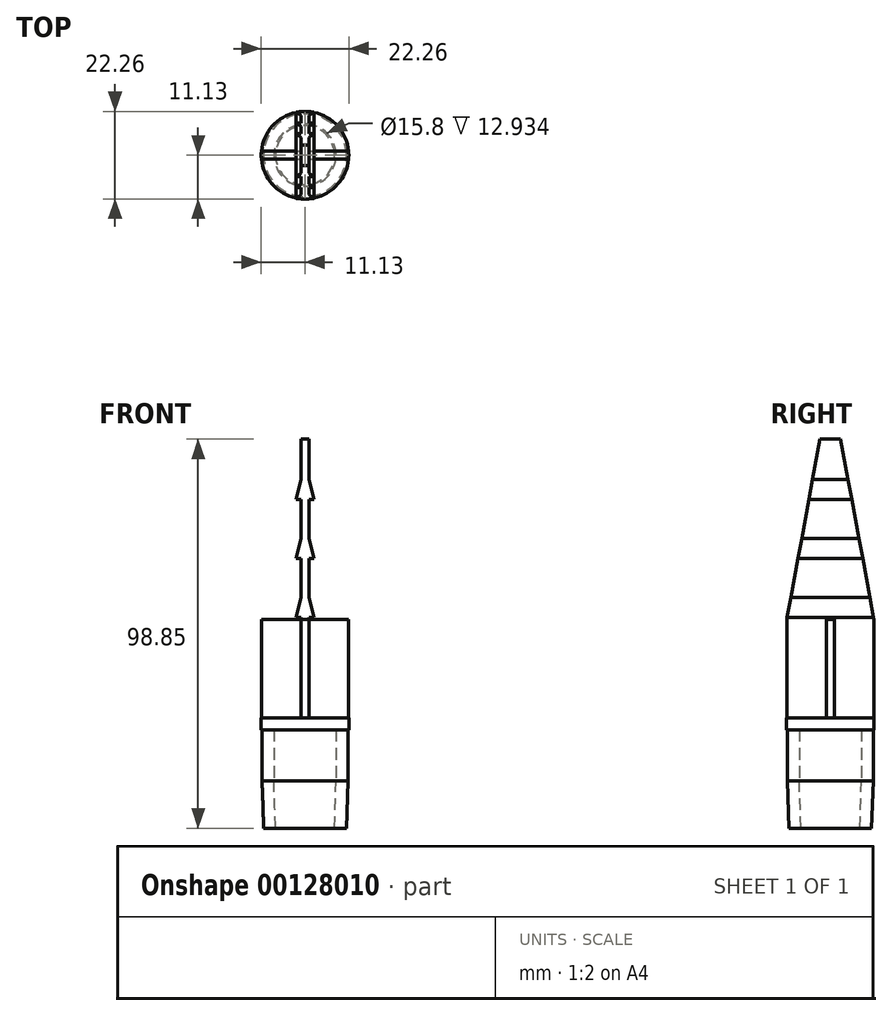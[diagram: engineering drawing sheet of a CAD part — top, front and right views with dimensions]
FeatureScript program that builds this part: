
annotation { "Feature Type Name" : "Feature", "Feature Type Description" : "" }
export const myFeature = defineFeature(function(context is Context, id is Id, definition is map)
    precondition{}
    {
        {
            var Q0;
            Q0=qCreatedBy(makeId("Top.planeOp"),FACE);
            var sketch = newSketch(context, id + "F0", { "sketchPlane" : qUnion([Q0])});
            skCircle(sketch, "E0", {"center": v(0, 0) * mm, "radius": 11.12 * mm});
            skSolve(sketch);
        }
        {
            var Q0;
            Q0=makeQuery(id+"F0.imprint","IMPRINT",FACE,{"disambiguationData":[TD([[makeQuery(id+"F0.imprint","IMPRINT",EDGE,{"derivedFrom":sQuery(id+"F0.wireOp",EDGE,"E0")}),1.0]])]});
            extrude(context, id + "F1", {"entities" : qUnion([Q0]), "depth" : 3 * mm});
        }
        {
            var Q0;
            Q0=makeQuery(id+"F1.opExtrude","CAP_FACE",FACE,{"disambiguationData":[OSD([sQuery(id+"F0.wireOp",EDGE,"E0")])],"isStart":false});
            var sketch = newSketch(context, id + "F2", { "sketchPlane" : qUnion([Q0])});
            skLineSegment(sketch, "E1.bottom", {"start": v(-11.08, 1) * mm, "end": v(-1, 1) * mm});
            skLineSegment(sketch, "E1.top", {"start": v(-11.08, -1) * mm, "end": v(-1, -1) * mm});
            skLineSegment(sketch, "E1.left", {"start": v(-11.08, 1) * mm, "end": v(-11.08, -1) * mm});
            skLineSegment(sketch, "E1.right", {"start": v(11.08, 1) * mm, "end": v(11.08, -1) * mm});
            skPoint(sketch, "E1.middle", {"position": v(0, 0) * mm});
            skLineSegment(sketch, "E2.bottom", {"start": v(-1, 11.08) * mm, "end": v(1, 11.08) * mm});
            skLineSegment(sketch, "E2.top", {"start": v(-1, -11.08) * mm, "end": v(1, -11.08) * mm});
            skLineSegment(sketch, "E2.left", {"start": v(-1, 11.08) * mm, "end": v(-1, 1) * mm});
            skLineSegment(sketch, "E2.right", {"start": v(1, 11.08) * mm, "end": v(1, 1) * mm});
            skLineSegment(sketch, "E3.trimOffspring", {"start": v(-1, -1) * mm, "end": v(-1, -11.08) * mm});
            skLineSegment(sketch, "E4.trimOffspring", {"start": v(1, -1) * mm, "end": v(11.08, -1) * mm});
            skLineSegment(sketch, "E5.trimOffspring", {"start": v(1, -1) * mm, "end": v(1, -11.08) * mm});
            skLineSegment(sketch, "E6.trimOffspring", {"start": v(1, 1) * mm, "end": v(11.08, 1) * mm});
            skSolve(sketch);
        }
        {
            var Q0;
            Q0=makeQuery(id+"F2.imprint","IMPRINT",FACE,{"disambiguationData":[TD([[makeQuery(id+"F2.imprint","IMPRINT",EDGE,{"derivedFrom":sQuery(id+"F2.wireOp",EDGE,"E1.bottom")}),-1.0]])]});
            extrude(context, id + "F3", {"entities" : qUnion([Q0]), "operationType" : NewBodyOperationType.ADD, "depth" : 25 * mm});
        }
        {
            var Q0;
            Q0=makeQuery(id+"F3.opExtrude","SWEPT_FACE",FACE,{"disambiguationData":[OSD([sQuery(id+"F2.wireOp",EDGE,"E5.trimOffspring")])]});
            var sketch = newSketch(context, id + "F4", { "sketchPlane" : qUnion([Q0])});
            skLineSegment(sketch, "E7", {"start": v(-11.08, 28) * mm, "end": v(-2.61, 73.85) * mm});
            skLineSegment(sketch, "E8", {"start": v(2.61, 73.85) * mm, "end": v(11.08, 28) * mm});
            skLineSegment(sketch, "E9", {"start": v(11.08, 28) * mm, "end": v(-11.08, 28) * mm});
            skLineSegment(sketch, "E10", {"start": v(-2.61, 73.85) * mm, "end": v(2.61, 73.85) * mm});
            skPoint(sketch, "E11.orphan", {"position": v(0, 88) * mm});
            skSolve(sketch);
        }
        {
            var Q0;
            {var subQ0=sQuery(id+"F4.wireOp",EDGE,"E7");Q0=makeQuery(id+"F4.imprint","IMPRINT",FACE,{"disambiguationData":[TD([[makeQuery(id+"F4.imprint","IMPRINT",EDGE,{"derivedFrom":subQ0}),-1.0]])]});}
            extrude(context, id + "F5", {"entities" : qUnion([Q0]), "operationType" : NewBodyOperationType.ADD, "oppositeDirection" : true, "depth" : 2 * mm});
        }
        {
            var Q0;
            Q0=qCreatedBy(makeId("Right.planeOp"),FACE);
            var sketch = newSketch(context, id + "F6", { "sketchPlane" : qUnion([Q0])});
            skLineSegment(sketch, "E12", {"start": v(0, 0) * mm, "end": v(0, 19.03) * mm, "construction": true});
            skSolve(sketch);
        }
        {
            var Q0;
            Q0=qCreatedBy(makeId("Front.planeOp"),FACE);
            var sketch = newSketch(context, id + "F7", { "sketchPlane" : qUnion([Q0])});
            skLineSegment(sketch, "E13", {"start": v(0, 37.5) * mm, "end": v(-2.3, 28.53) * mm});
            skLineSegment(sketch, "E14", {"start": v(-2.3, 28.53) * mm, "end": v(2.3, 28.53) * mm});
            skLineSegment(sketch, "E15", {"start": v(2.3, 28.53) * mm, "end": v(0, 37.5) * mm});
            skLineSegment(sketch, "E16.0.1.0", {"start": v(0, 52.5) * mm, "end": v(-2.3, 43.53) * mm});
            skLineSegment(sketch, "E16.0.1.1", {"start": v(2.3, 43.53) * mm, "end": v(0, 52.5) * mm});
            skLineSegment(sketch, "E16.0.1.2", {"start": v(-2.3, 43.53) * mm, "end": v(2.3, 43.53) * mm});
            skLineSegment(sketch, "E16.0.2.0", {"start": v(0, 67.5) * mm, "end": v(-2.3, 58.53) * mm});
            skLineSegment(sketch, "E16.0.2.1", {"start": v(2.3, 58.53) * mm, "end": v(0, 67.5) * mm});
            skLineSegment(sketch, "E16.0.2.2", {"start": v(-2.3, 58.53) * mm, "end": v(2.3, 58.53) * mm});
            skLineSegment(sketch, "E16.direction1", {"start": v(-2.3, 28.53) * mm, "end": v(-27.3, 28.53) * mm, "construction": true});
            skLineSegment(sketch, "E16.direction2", {"start": v(-2.3, 28.53) * mm, "end": v(-2.3, 43.53) * mm, "construction": true});
            skSolve(sketch);
        }
        {
            var Q0;
            Q0 = qSketchRegion(id + "F7", true);
            var Q1;
            Q1=makeQuery(id+"F5.opExtrude","SWEPT_FACE",FACE,{"disambiguationData":[OSD([sQuery(id+"F4.wireOp",EDGE,"E7")])]});
            var Q2;
            Q2=makeQuery(id+"F5.opExtrude","SWEPT_FACE",FACE,{"disambiguationData":[OSD([sQuery(id+"F4.wireOp",EDGE,"E8")])]});
            extrude(context, id + "F8", {"entities" : qUnion([Q0]), "operationType" : NewBodyOperationType.ADD, "endBound" : BoundingType.UP_TO_SURFACE, "endBoundEntityFace" : qUnion([Q1]), "depth" : 25 * mm, "hasSecondDirection" : true, "secondDirectionBound" : SecondDirectionBoundingType.UP_TO_SURFACE, "secondDirectionOppositeDirection" : true, "secondDirectionBoundEntityFace" : qUnion([Q2]), "secondDirectionDepth" : 25 * mm});
        }
        {
            var Q0;
            Q0=qCreatedBy(makeId("Front.planeOp"),FACE);
            var sketch = newSketch(context, id + "F9", { "sketchPlane" : qUnion([Q0])});
            skLineSegment(sketch, "E17", {"start": v(10.9, 0) * mm, "end": v(10.9, -12.93) * mm});
            skLineSegment(sketch, "E18", {"start": v(10.9, -12.93) * mm, "end": v(10.5, -25) * mm});
            skLineSegment(sketch, "E19", {"start": v(10.5, -25) * mm, "end": v(7.5, -25) * mm});
            skLineSegment(sketch, "E20", {"start": v(7.5, -25) * mm, "end": v(7.9, -12.93) * mm});
            skLineSegment(sketch, "E21", {"start": v(7.9, -12.93) * mm, "end": v(7.9, 0) * mm});
            skLineSegment(sketch, "E22", {"start": v(7.9, 0) * mm, "end": v(10.9, 0) * mm});
            skSolve(sketch);
        }
        {
            var Q0;
            Q0=makeQuery(id+"F9.imprint","IMPRINT",FACE,{"disambiguationData":[TD([[makeQuery(id+"F9.imprint","IMPRINT",EDGE,{"derivedFrom":sQuery(id+"F9.wireOp",EDGE,"E17")}),-1.0]])]});
            var Q1;
            Q1=sQuery(id+"F6.wireOp",EDGE,"E12");
            revolve(context, id + "F10", {"operationType" : NewBodyOperationType.ADD, "entities" : qUnion([Q0]), "axis" : qUnion([Q1]), "revolveType" : RevolveType.FULL});
        }
    });
